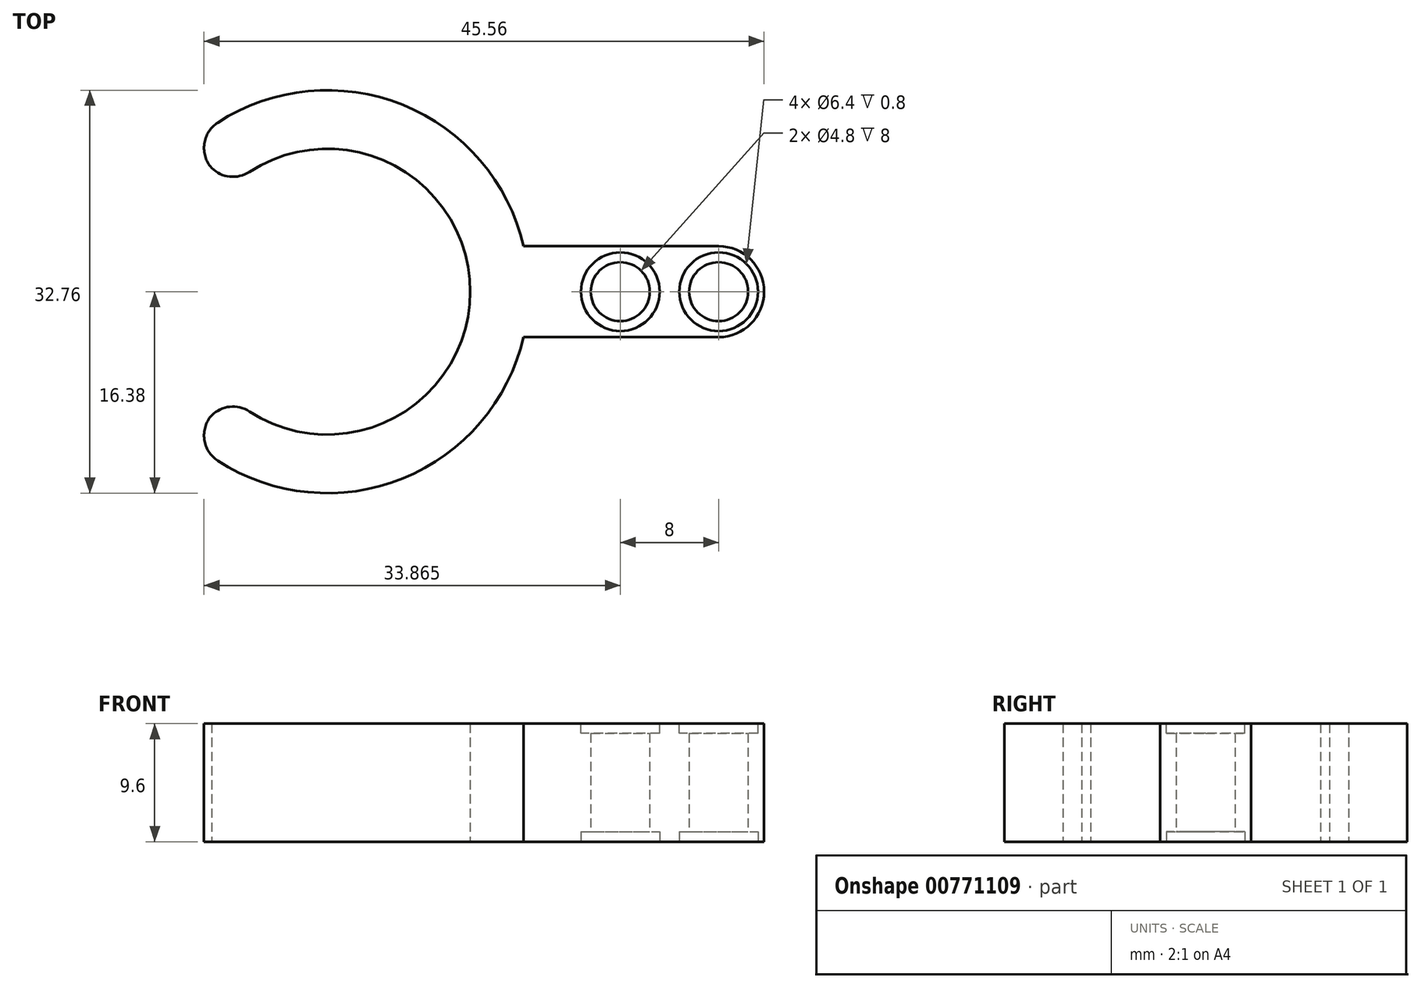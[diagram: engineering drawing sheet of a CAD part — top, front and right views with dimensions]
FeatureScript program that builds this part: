
annotation { "Feature Type Name" : "Feature", "Feature Type Description" : "" }
export const myFeature = defineFeature(function(context is Context, id is Id, definition is map)
    precondition{}
    {
        {
            var Q0;
            Q0=qCreatedBy(makeId("Top.planeOp"),FACE);
            var sketch = newSketch(context, id + "F0", { "sketchPlane" : qUnion([Q0])});
            skArc(sketch, "E0", {"start": v(-7.94, 8.49) * mm, "mid": v(11.62, 0) * mm, "end": v(-7.94, -8.49) * mm});
            skArc(sketch, "E1", {"start": v(-11.2, 11.97) * mm, "mid": v(16.38, 0) * mm, "end": v(-11.2, -11.97) * mm});
            skLineSegment(sketch, "E2", {"start": v(-11.2, -11.97) * mm, "end": v(-7.94, -8.49) * mm});
            skLineSegment(sketch, "E3", {"start": v(-11.2, 11.97) * mm, "end": v(-7.94, 8.49) * mm});
            skCircle(sketch, "E4", {"center": v(-7.94, 0) * mm, "radius": 11.11 * mm, "construction": true});
            skSolve(sketch);
        }
        {
            var Q0;
            Q0=qSketchRegion(id+"F0",true);
            extrude(context, id + "F1", {"entities" : qUnion([Q0]), "depth" : 9.6 * mm, "offsetDistance" : 25.4 * mm});
        }
        {
            var Q0;
            Q0=qCreatedBy(makeId("Top.planeOp"),FACE);
            var sketch = newSketch(context, id + "F2", { "sketchPlane" : qUnion([Q0])});
            skLineSegment(sketch, "E5", {"start": v(15.96, 3.7) * mm, "end": v(31.83, 3.7) * mm});
            skLineSegment(sketch, "E6", {"start": v(15.96, -3.7) * mm, "end": v(31.83, -3.7) * mm});
            skArc(sketch, "E7", {"start": v(31.83, 3.7) * mm, "mid": v(35.53, 0) * mm, "end": v(31.83, -3.7) * mm});
            skCircle(sketch, "E8", {"center": v(31.83, 0) * mm, "radius": 2.4 * mm});
            skCircle(sketch, "E9", {"center": v(23.83, 0) * mm, "radius": 2.4 * mm});
            skArc(sketch, "E10", {"start": v(15.96, -3.7) * mm, "mid": v(16.38, 0) * mm, "end": v(15.96, 3.7) * mm});
            skSolve(sketch);
        }
        {
            var Q0;
            Q0=qSketchRegion(id+"F2",true);
            var Q1;
            Q1=makeQuery(id+"F1.opExtrude","CAP_FACE",FACE,{"disambiguationData":[OSD([sQuery(id+"F0.wireOp",EDGE,"E0"),sQuery(id+"F0.wireOp",EDGE,"E1"),sQuery(id+"F0.wireOp",EDGE,"E2"),sQuery(id+"F0.wireOp",EDGE,"E3")])],"isStart":false});
            extrude(context, id + "F3", {"entities" : qUnion([Q0]), "operationType" : NewBodyOperationType.ADD, "endBound" : BoundingType.UP_TO_SURFACE, "depth" : 25.4 * mm, "endBoundEntityFace" : qUnion([Q1]), "offsetDistance" : 25.4 * mm});
        }
        {
            var Q0;
            Q0=makeQuery(id+"F1.opExtrude","SWEPT_EDGE",EDGE,{"disambiguationData":[OSD([sQuery(id+"F0.wireOp",EDGE,"E1"),sQuery(id+"F0.wireOp",EDGE,"E3")])]});
            var Q1;
            Q1=makeQuery(id+"F1.opExtrude","SWEPT_EDGE",EDGE,{"disambiguationData":[OSD([sQuery(id+"F0.wireOp",EDGE,"E1"),sQuery(id+"F0.wireOp",EDGE,"E2")])]});
            var Q2;
            Q2=makeQuery(id+"F1.opExtrude","SWEPT_EDGE",EDGE,{"disambiguationData":[OSD([sQuery(id+"F0.wireOp",EDGE,"E0"),sQuery(id+"F0.wireOp",EDGE,"E3")])]});
            var Q3;
            Q3=makeQuery(id+"F1.opExtrude","SWEPT_EDGE",EDGE,{"disambiguationData":[OSD([sQuery(id+"F0.wireOp",EDGE,"E0"),sQuery(id+"F0.wireOp",EDGE,"E2")])]});
            fillet(context, id + "F4", {"entities" : qUnion([Q0, Q1, Q2, Q3]), "radius" : 2.45 * mm, "tangentPropagation" : true, "allowEdgeOverflow" : false});
        }
        {
            var Q0;
            Q0=makeQuery(id+"F3.boolean.opBoolean","MERGE",FACE,{"derivedFrom":[makeQuery(id+"F1.opExtrude","CAP_FACE",FACE,{"disambiguationData":[OSD([sQuery(id+"F0.wireOp",EDGE,"E0"),sQuery(id+"F0.wireOp",EDGE,"E1"),sQuery(id+"F0.wireOp",EDGE,"E2"),sQuery(id+"F0.wireOp",EDGE,"E3")])],"isStart":false}),makeQuery(id+"F3.opExtrude","CAP_FACE",FACE,{"disambiguationData":[OSD([sQuery(id+"F2.wireOp",EDGE,"E5"),sQuery(id+"F2.wireOp",EDGE,"E6"),sQuery(id+"F2.wireOp",EDGE,"E7"),sQuery(id+"F2.wireOp",EDGE,"E8"),sQuery(id+"F2.wireOp",EDGE,"E9"),sQuery(id+"F2.wireOp",EDGE,"E10")])],"isStart":false})]});
            var sketch = newSketch(context, id + "F5", { "sketchPlane" : qUnion([Q0])});
            skCircle(sketch, "E11", {"center": v(23.83, 0) * mm, "radius": 3.2 * mm});
            skCircle(sketch, "E12", {"center": v(31.83, 0) * mm, "radius": 3.2 * mm});
            skSolve(sketch);
        }
        {
            var Q0;
            Q0 = qSketchRegion(id + "F5", true);
            extrude(context, id + "F6", {"entities" : qUnion([Q0]), "operationType" : NewBodyOperationType.REMOVE, "oppositeDirection" : true, "depth" : .8 * mm, "offsetDistance" : 25.4 * mm});
        }
        {
            var Q0;
            Q0=makeQuery(id+"F3.boolean.opBoolean","MERGE",FACE,{"derivedFrom":[makeQuery(id+"F1.opExtrude","CAP_FACE",FACE,{"disambiguationData":[OSD([sQuery(id+"F0.wireOp",EDGE,"E0"),sQuery(id+"F0.wireOp",EDGE,"E1"),sQuery(id+"F0.wireOp",EDGE,"E2"),sQuery(id+"F0.wireOp",EDGE,"E3")])],"isStart":true}),makeQuery(id+"F3.opExtrude","CAP_FACE",FACE,{"disambiguationData":[OSD([sQuery(id+"F2.wireOp",EDGE,"E5"),sQuery(id+"F2.wireOp",EDGE,"E6"),sQuery(id+"F2.wireOp",EDGE,"E7"),sQuery(id+"F2.wireOp",EDGE,"E8"),sQuery(id+"F2.wireOp",EDGE,"E9"),sQuery(id+"F2.wireOp",EDGE,"E10")])],"isStart":true})]});
            var sketch = newSketch(context, id + "F7", { "sketchPlane" : qUnion([Q0])});
            skCircle(sketch, "E13", {"center": v(23.83, 0) * mm, "radius": 3.2 * mm});
            skCircle(sketch, "E14", {"center": v(31.83, 0) * mm, "radius": 3.2 * mm});
            skSolve(sketch);
        }
        {
            var Q0;
            Q0 = qSketchRegion(id + "F7", true);
            extrude(context, id + "F8", {"entities" : qUnion([Q0]), "operationType" : NewBodyOperationType.REMOVE, "oppositeDirection" : true, "depth" : .8 * mm, "offsetDistance" : 25.4 * mm});
        }
    });
